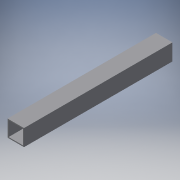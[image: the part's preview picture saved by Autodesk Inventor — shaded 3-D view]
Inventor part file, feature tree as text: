
AUTODESK INVENTOR PART (.ipt)
format: ipt  version: 2016 (Build 200138000, 138)  size: 91,648 bytes
history: native  units: in
note: dims shown in document units (in); Inventor stores cm internally (conversion verified against a paired STEP export)
features: extrude x1, sketch x1
ambient origin geometry x8: Origin, YZ Plane, XZ Plane, XY Plane, X Axis, Y Axis, Z Axis, Center Point
bodies: Solid1 (feature_tree)
feature tree (2):
  extrude  "Extrusion1"  Depth=1.0in
  sketch  "Sketch1"  dims[d0=1.0in d1=1.0in d2=0.0625in d3=9.0in d4=0.0in]
